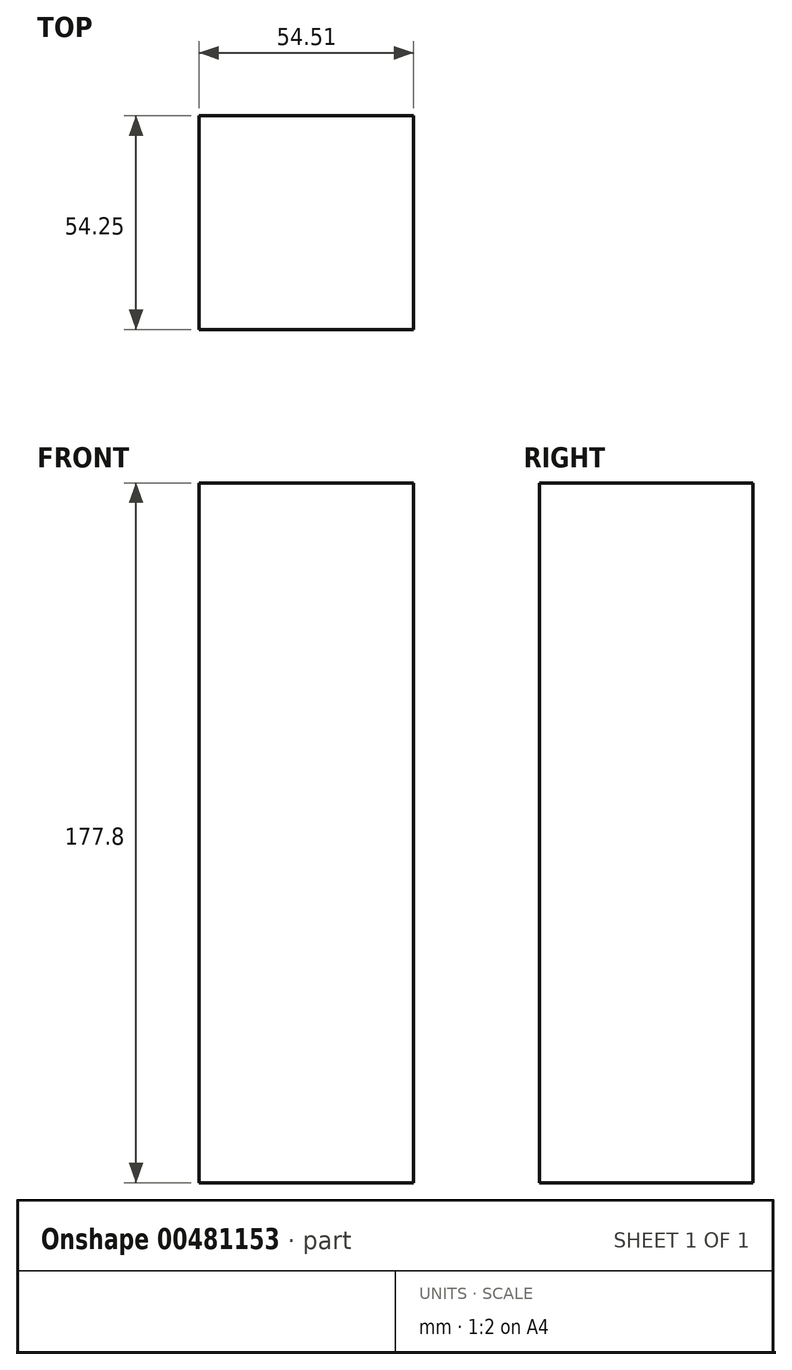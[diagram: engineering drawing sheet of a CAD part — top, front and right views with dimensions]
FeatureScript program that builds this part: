
annotation { "Feature Type Name" : "Feature", "Feature Type Description" : "" }
export const myFeature = defineFeature(function(context is Context, id is Id, definition is map)
    precondition{}
    {
        {
            var Q0;
            Q0=qCreatedBy(makeId("Top.planeOp"),FACE);
            var sketch = newSketch(context, id + "F0", { "sketchPlane" : qUnion([Q0])});
            skLineSegment(sketch, "E0.bottom", {"start": v(0.2, 2.5) * mm, "end": v(-54.3, 2.5) * mm});
            skLineSegment(sketch, "E0.top", {"start": v(0.2, 56.75) * mm, "end": v(-54.3, 56.75) * mm});
            skLineSegment(sketch, "E0.left", {"start": v(0.2, 2.5) * mm, "end": v(0.2, 56.75) * mm});
            skLineSegment(sketch, "E0.right", {"start": v(-54.3, 2.5) * mm, "end": v(-54.3, 56.75) * mm});
            skSolve(sketch);
        }
        {
            var Q0;
            Q0=qSketchRegion(id+"F0",true);
            extrude(context, id + "F1", {"entities" : qUnion([Q0]), "depth" : 177.8 * mm});
        }
    });
